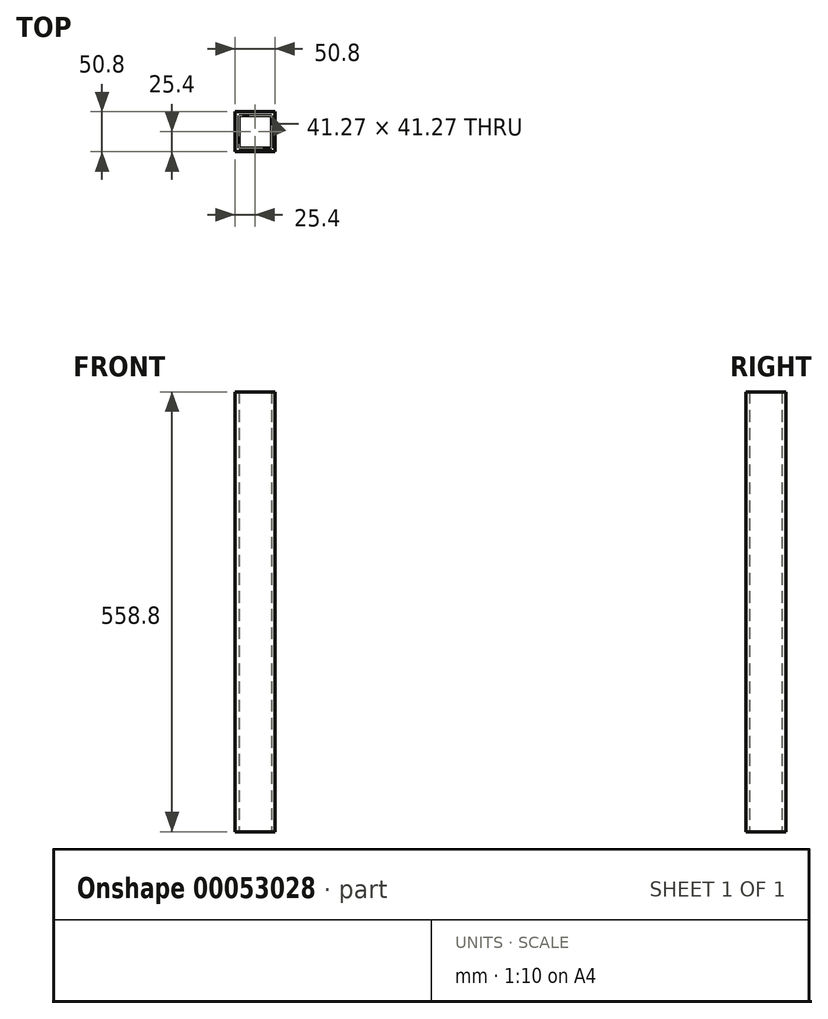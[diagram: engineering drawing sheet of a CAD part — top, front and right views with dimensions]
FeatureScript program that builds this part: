
annotation { "Feature Type Name" : "Feature", "Feature Type Description" : "" }
export const myFeature = defineFeature(function(context is Context, id is Id, definition is map)
    precondition{}
    {
        {
            var Q0;
            Q0=qCreatedBy(makeId("Top.planeOp"),FACE);
            var sketch = newSketch(context, id + "F0", { "sketchPlane" : qUnion([Q0])});
            skLineSegment(sketch, "E0.bottom", {"start": v(0, 0) * mm, "end": v(-50.8, 0) * mm});
            skLineSegment(sketch, "E0.top", {"start": v(0, -50.8) * mm, "end": v(-50.8, -50.8) * mm});
            skLineSegment(sketch, "E0.left", {"start": v(0, 0) * mm, "end": v(0, -50.8) * mm});
            skLineSegment(sketch, "E0.right", {"start": v(-50.8, 0) * mm, "end": v(-50.8, -50.8) * mm});
            skLineSegment(sketch, "E1.bottom", {"start": v(-46.04, -4.76) * mm, "end": v(-4.76, -4.76) * mm});
            skLineSegment(sketch, "E1.top", {"start": v(-46.04, -46.04) * mm, "end": v(-4.76, -46.04) * mm});
            skLineSegment(sketch, "E1.left", {"start": v(-46.04, -4.76) * mm, "end": v(-46.04, -46.04) * mm});
            skLineSegment(sketch, "E1.right", {"start": v(-4.76, -4.76) * mm, "end": v(-4.76, -46.04) * mm});
            skSolve(sketch);
        }
        {
            var Q0;
            Q0=makeQuery(id+"F0.imprint","IMPRINT",FACE,{"disambiguationData":[TD([[makeQuery(id+"F0.imprint","IMPRINT",EDGE,{"derivedFrom":sQuery(id+"F0.wireOp",EDGE,"E0.bottom")}),1.0]])]});
            extrude(context, id + "F1", {"entities" : qUnion([Q0]), "depth" : 558.8 * mm});
        }
    });
